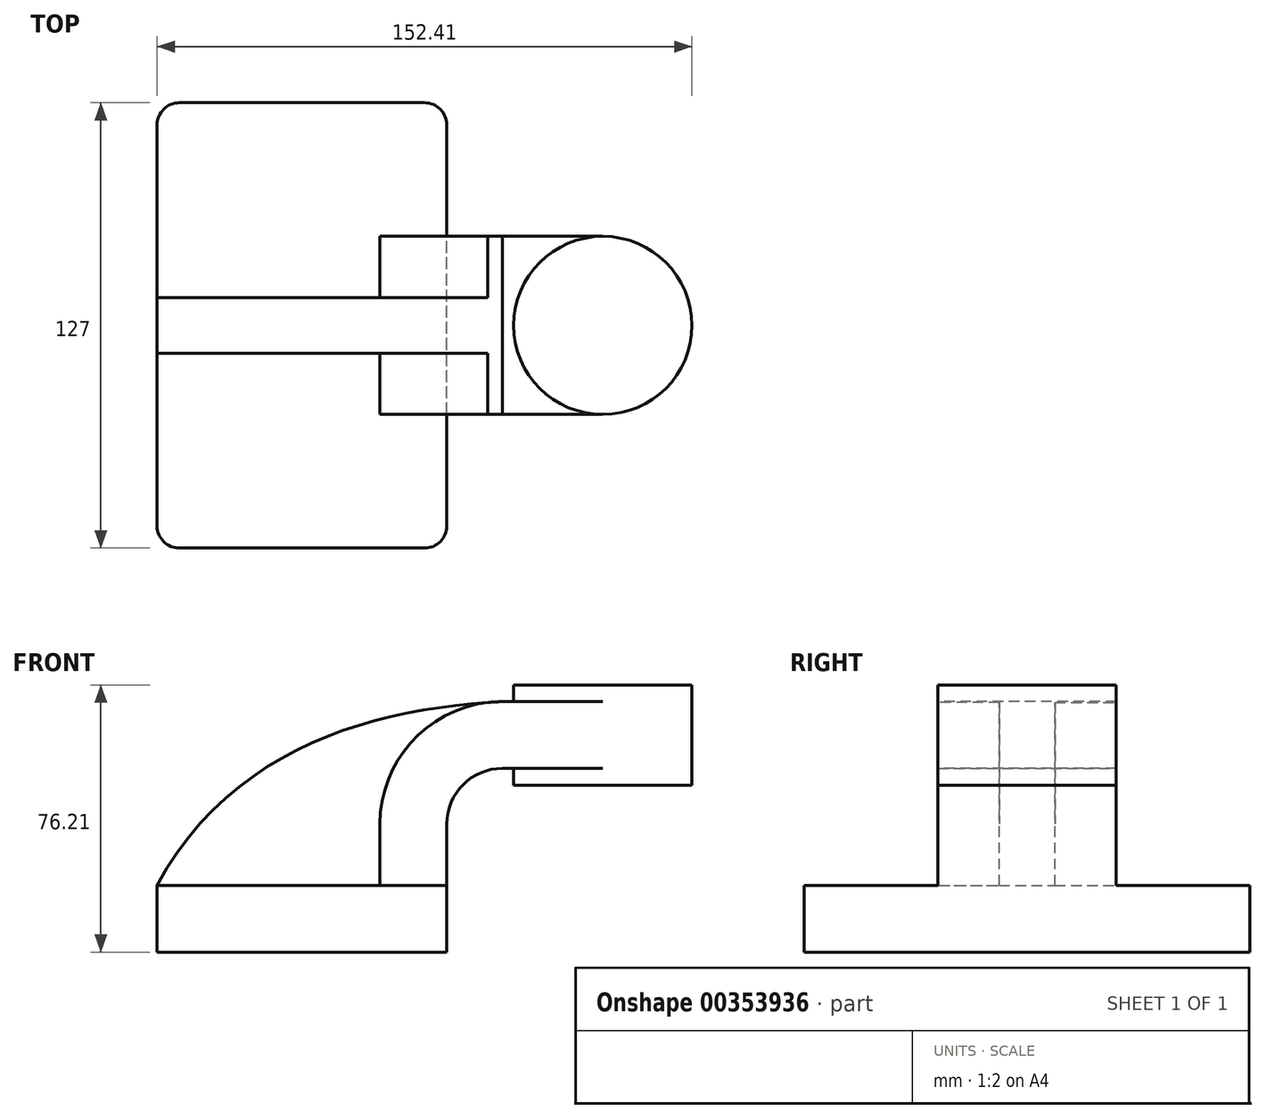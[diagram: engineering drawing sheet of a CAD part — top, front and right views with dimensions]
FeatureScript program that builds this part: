
annotation { "Feature Type Name" : "Feature", "Feature Type Description" : "" }
export const myFeature = defineFeature(function(context is Context, id is Id, definition is map)
    precondition{}
    {
        {
            var Q0;
            Q0=qCreatedBy(makeId("Front.planeOp"),FACE);
            var sketch = newSketch(context, id + "F0", { "sketchPlane" : qUnion([Q0])});
            skLineSegment(sketch, "E0.bottom", {"start": v(-41.28, 9.52) * mm, "end": v(41.28, 9.53) * mm});
            skLineSegment(sketch, "E0.top", {"start": v(-41.28, -9.53) * mm, "end": v(41.28, -9.53) * mm});
            skLineSegment(sketch, "E0.left", {"start": v(-41.28, 9.52) * mm, "end": v(-41.28, -9.53) * mm});
            skLineSegment(sketch, "E0.right", {"start": v(41.28, 9.53) * mm, "end": v(41.28, -9.52) * mm});
            skPoint(sketch, "E0.middle", {"position": v(0, 0) * mm});
            skLineSegment(sketch, "E1", {"start": v(41.27, 9.53) * mm, "end": v(41.27, 27) * mm});
            skArc(sketch, "E2", {"start": v(41.27, 27) * mm, "mid": v(45.92, 38.23) * mm, "end": v(57.15, 42.88) * mm});
            skLineSegment(sketch, "E3", {"start": v(57.15, 42.88) * mm, "end": v(85.72, 42.88) * mm});
            skLineSegment(sketch, "E4.bottom", {"start": v(111.12, 38.1) * mm, "end": v(60.32, 38.1) * mm});
            skLineSegment(sketch, "E4.top", {"start": v(111.12, 66.68) * mm, "end": v(60.32, 66.68) * mm});
            skLineSegment(sketch, "E4.left", {"start": v(111.12, 38.1) * mm, "end": v(111.12, 66.68) * mm});
            skLineSegment(sketch, "E4.right", {"start": v(60.32, 38.1) * mm, "end": v(60.32, 66.68) * mm});
            skPoint(sketch, "E4.middle", {"position": v(85.72, 52.39) * mm});
            skLineSegment(sketch, "E5.0", {"start": v(57.15, 61.93) * mm, "end": v(85.72, 61.93) * mm});
            skArc(sketch, "E5.1", {"start": v(22.22, 27) * mm, "mid": v(32.45, 51.7) * mm, "end": v(57.15, 61.93) * mm});
            skLineSegment(sketch, "E5.2", {"start": v(22.22, 9.53) * mm, "end": v(22.22, 27) * mm});
            skLineSegment(sketch, "E6", {"start": v(85.72, 66.68) * mm, "end": v(85.72, 38.1) * mm});
            skFitSpline(sketch, "E7", {"points": [v(-41.28, 9.52) * mm, v(57.15, 61.93) * mm], "startDerivative": vector(64.97, 119.88) * mm, "endDerivative": vector(107.79, 5.59) * mm});
            skSolve(sketch);
        }
        {
            var Q0;
            Q0=makeQuery(id+"F0.imprint","IMPRINT",FACE,{"disambiguationData":[TD([[makeQuery(id+"F0.imprint","IMPRINT",EDGE,{"derivedFrom":sQuery(id+"F0.wireOp",EDGE,"E0.top")}),1.0]])]});
            extrude(context, id + "F1", {"entities" : qUnion([Q0]), "endBound" : BoundingType.SYMMETRIC, "depth" : 127 * mm});
        }
        {
            var Q0;
            {var subQ4=sQuery(id+"F0.wireOp",EDGE,"E1");Q0=makeQuery(id+"F0.imprint","IMPRINT",FACE,{"disambiguationData":[TD([[makeQuery(id+"F0.imprint","IMPRINT",EDGE,{"derivedFrom":subQ4}),1.0]])]});}
            extrude(context, id + "F2", {"entities" : qUnion([Q0]), "operationType" : NewBodyOperationType.ADD, "endBound" : BoundingType.SYMMETRIC, "depth" : 50.8 * mm});
        }
        {
            var Q0;
            {var subQ3=sQuery(id+"F0.wireOp",EDGE,"E5.2");Q0=makeQuery(id+"F0.imprint","IMPRINT",FACE,{"disambiguationData":[TD([[makeQuery(id+"F0.imprint","IMPRINT",EDGE,{"derivedFrom":subQ3}),1.0]])]});}
            extrude(context, id + "F3", {"entities" : qUnion([Q0]), "operationType" : NewBodyOperationType.ADD, "endBound" : BoundingType.SYMMETRIC, "depth" : 15.88 * mm});
        }
        {
            var Q0;
            {var subQ0=sQuery(id+"F0.wireOp",EDGE,"E6");var subQ1=sQuery(id+"F0.wireOp",EDGE,"E3");var subQ2=makeQuery(id+"F0.imprint","INTERSECT",VERTEX,{"derivedFrom":[subQ1,subQ0]});Q0=makeQuery(id+"F0.imprint","IMPRINT",FACE,{"disambiguationData":[TD([[makeQuery(id+"F0.imprint","IMPRINT",EDGE,{"disambiguationData":[TD([[subQ2,1.0]])],"derivedFrom":subQ1}),1.0]])]});}
            extrude(context, id + "F4", {"entities" : qUnion([Q0]), "operationType" : NewBodyOperationType.ADD, "endBound" : BoundingType.SYMMETRIC, "depth" : 50.8 * mm});
        }
        {
            var Q0;
            {var subQ4=sQuery(id+"F0.wireOp",EDGE,"E4.left");Q0=makeQuery(id+"F0.imprint","IMPRINT",FACE,{"disambiguationData":[TD([[makeQuery(id+"F0.imprint","IMPRINT",EDGE,{"derivedFrom":subQ4}),1.0]])]});}
            var Q1;
            Q1=sQuery(id+"F0.wireOp",EDGE,"E6");
            revolve(context, id + "F5", {"operationType" : NewBodyOperationType.ADD, "entities" : qUnion([Q0]), "axis" : qUnion([Q1]), "revolveType" : RevolveType.FULL});
        }
        {
            var Q0;
            Q0=makeQuery(id+"F1.opExtrude","CAP_EDGE",EDGE,{"disambiguationData":[OSD([sQuery(id+"F0.wireOp",EDGE,"E0.right")])],"isStart":false});
            var Q1;
            Q1=makeQuery(id+"F1.opExtrude","CAP_EDGE",EDGE,{"disambiguationData":[OSD([sQuery(id+"F0.wireOp",EDGE,"E0.right")])],"isStart":true});
            var Q2;
            Q2=makeQuery(id+"F1.opExtrude","CAP_EDGE",EDGE,{"disambiguationData":[OSD([sQuery(id+"F0.wireOp",EDGE,"E0.left")])],"isStart":true});
            var Q3;
            Q3=makeQuery(id+"F1.opExtrude","CAP_EDGE",EDGE,{"disambiguationData":[OSD([sQuery(id+"F0.wireOp",EDGE,"E0.left")])],"isStart":false});
            fillet(context, id + "F6", {"entities" : qUnion([Q0, Q1, Q2, Q3]), "radius" : 6.35 * mm, "tangentPropagation" : true, "allowEdgeOverflow" : false});
        }
    });
